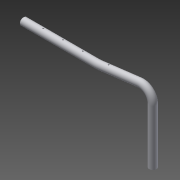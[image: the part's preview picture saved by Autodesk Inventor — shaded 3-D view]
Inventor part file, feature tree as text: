
AUTODESK INVENTOR PART (.ipt)
format: ipt  version: 2015 (Build 190159000, 159)  size: 192,512 bytes
history: native  units: mm
features: sketch x5, other x4, extrude x2, shell x1
ambient origin geometry x8: Origin, YZ Plane, XZ Plane, XY Plane, X Axis, Y Axis, Z Axis, Center Point
bodies: Body1 (feature_tree)
feature tree (12):
  other  "Bryła1"
  extrude  "Wyciągnięcie proste1"  Depth=32.0mm
  shell  "Skorupa1"  Thickness=815.0mm
  other  "Gięcie części1"
  sketch  "Szkic7"
  other  "Płaszczyzna konstrukcyjna4"
  other  "Gięcie części2"
  extrude  "Wyciągnięcie proste3"  Depth=2.0mm
  sketch  "Szkic1"
  sketch  "Szkic4"
  sketch  "Szkic8"
  sketch  "Szkic9"
